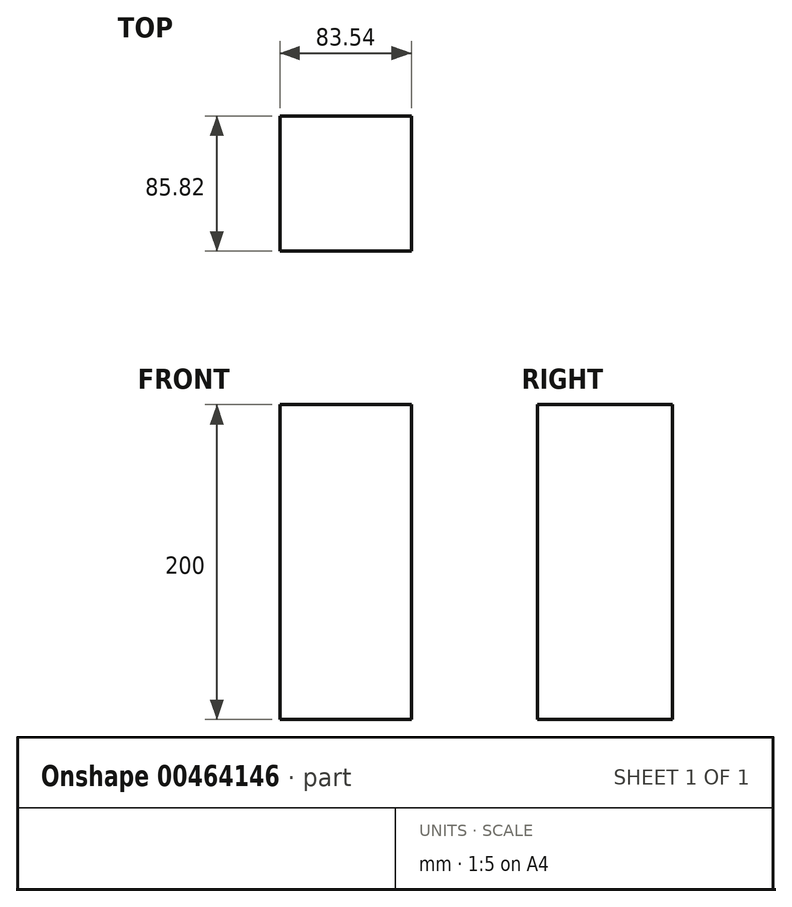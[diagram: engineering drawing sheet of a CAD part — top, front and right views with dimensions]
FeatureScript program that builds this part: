
annotation { "Feature Type Name" : "Feature", "Feature Type Description" : "" }
export const myFeature = defineFeature(function(context is Context, id is Id, definition is map)
    precondition{}
    {
        {
            var Q0;
            Q0=qCreatedBy(makeId("Top.planeOp"),FACE);
            var sketch = newSketch(context, id + "F0", { "sketchPlane" : qUnion([Q0])});
            skLineSegment(sketch, "E0.bottom", {"start": v(41.77, -42.91) * mm, "end": v(-41.77, -42.91) * mm});
            skLineSegment(sketch, "E0.top", {"start": v(41.77, 42.91) * mm, "end": v(-41.77, 42.91) * mm});
            skLineSegment(sketch, "E0.left", {"start": v(41.77, -42.91) * mm, "end": v(41.77, 42.91) * mm});
            skLineSegment(sketch, "E0.right", {"start": v(-41.77, -42.91) * mm, "end": v(-41.77, 42.91) * mm});
            skPoint(sketch, "E0.middle", {"position": v(0, 0) * mm});
            skSolve(sketch);
        }
        {
            var Q0;
            Q0=makeQuery(id+"F0.imprint","IMPRINT",FACE,{"disambiguationData":[TD([[makeQuery(id+"F0.imprint","IMPRINT",EDGE,{"derivedFrom":sQuery(id+"F0.wireOp",EDGE,"E0.bottom")}),-1.0]])]});
            extrude(context, id + "F1", {"entities" : qUnion([Q0]), "depth" : 200 * mm});
        }
    });
